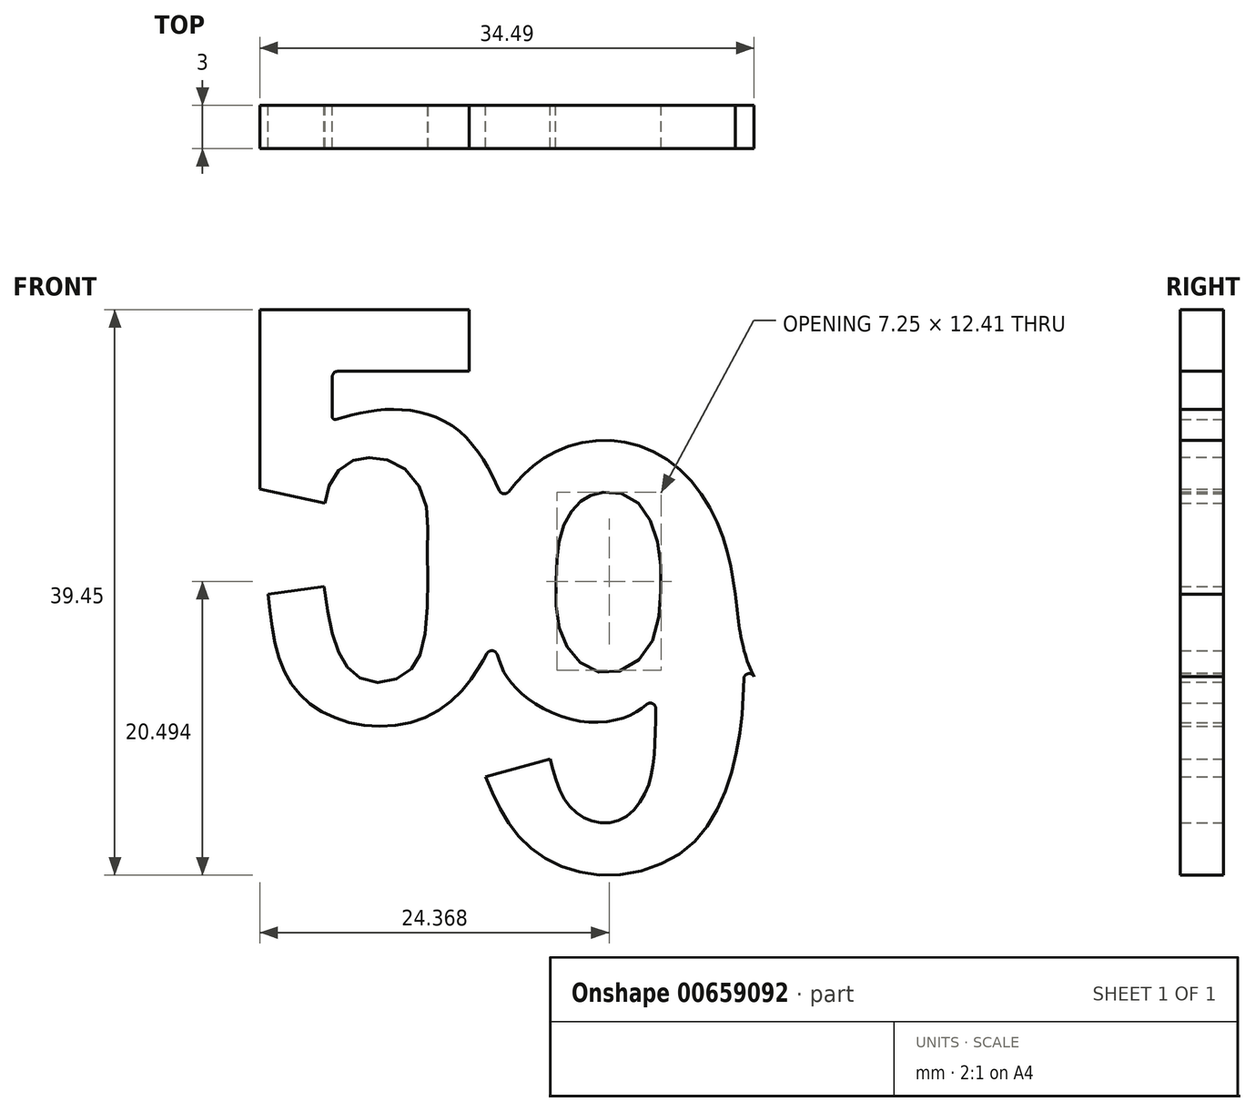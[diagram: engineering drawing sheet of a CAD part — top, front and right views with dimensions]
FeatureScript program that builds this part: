
annotation { "Feature Type Name" : "Feature", "Feature Type Description" : "" }
export const myFeature = defineFeature(function(context is Context, id is Id, definition is map)
    precondition{}
    {
        {
            var Q0;
            Q0=qCreatedBy(makeId("Front.planeOp"),FACE);
            var sketch = newSketch(context, id + "F0", { "sketchPlane" : qUnion([Q0])});
            skLineSegment(sketch, "E0", {"start": v(-24.18, 19.03) * mm, "end": v(-9.57, 19.03) * mm});
            skLineSegment(sketch, "E1", {"start": v(-24.18, 19.03) * mm, "end": v(-24.18, 6.52) * mm});
            skLineSegment(sketch, "E2", {"start": v(-24.18, 6.52) * mm, "end": v(-19.64, 5.52) * mm});
            skLineSegment(sketch, "E3", {"start": v(-9.57, 19.03) * mm, "end": v(-9.57, 14.73) * mm});
            skLineSegment(sketch, "E4", {"start": v(-9.57, 14.73) * mm, "end": v(-18.75, 14.73) * mm});
            skLineSegment(sketch, "E5", {"start": v(-19.13, 14.34) * mm, "end": v(-19.13, 11.56) * mm});
            skLineSegment(sketch, "E6", {"start": v(-19.7, -0.28) * mm, "end": v(-23.62, -0.8) * mm});
            skLineSegment(sketch, "E7", {"start": v(8.43, 19.03) * mm, "end": v(23.04, 19.03) * mm});
            skLineSegment(sketch, "E8", {"start": v(8.43, 19.03) * mm, "end": v(8.43, 6.52) * mm});
            skLineSegment(sketch, "E9", {"start": v(8.43, 6.52) * mm, "end": v(12.97, 5.52) * mm});
            skLineSegment(sketch, "E10", {"start": v(23.04, 19.03) * mm, "end": v(23.04, 14.73) * mm});
            skLineSegment(sketch, "E11", {"start": v(23.04, 14.73) * mm, "end": v(13.87, 14.73) * mm});
            skLineSegment(sketch, "E12", {"start": v(13.48, 14.34) * mm, "end": v(13.48, 11.56) * mm});
            skLineSegment(sketch, "E13", {"start": v(12.9, -0.28) * mm, "end": v(8.99, -0.8) * mm});
            skFitSpline(sketch, "E14", {"points": [v(-23.62, -0.8) * mm, v(-22.6, -5.93) * mm, v(-20.1, -8.86) * mm, v(-15.7, -10.03) * mm, v(-11.16, -8.56) * mm, v(-8.72, -5.62) * mm, v(-8.17, -4.64) * mm], "startDerivative": vector(3.05, -27.84) * mm, "endDerivative": vector(4.84, 9.1) * mm});
            skFitSpline(sketch, "E15", {"points": [v(-19.7, -0.28) * mm, v(-19.17, -3.5) * mm, v(-18.4, -5.44) * mm, v(-17.3, -6.6) * mm, v(-15.43, -6.96) * mm, v(-13.7, -6.12) * mm, v(-12.88, -4.67) * mm, v(-12.49, -0.89) * mm, v(-12.49, 3.08) * mm, v(-12.67, 5.78) * mm, v(-14.23, 8.06) * mm, v(-16.23, 8.7) * mm, v(-17.75, 8.5) * mm, v(-19.11, 7.28) * mm, v(-19.64, 5.52) * mm], "startDerivative": vector(5.37, -39.95) * mm, "endDerivative": vector(-5.42, -28.28) * mm});
            skFitSpline(sketch, "E16", {"points": [v(-19.13, 11.3) * mm, v(-16.5, 11.94) * mm, v(-13.79, 12) * mm, v(-10.94, 11.04) * mm, v(-8.67, 8.72) * mm, v(-7.35, 6.14) * mm], "startDerivative": vector(13.56, 3.87) * mm, "endDerivative": vector(5.77, -13.07) * mm});
            skFitSpline(sketch, "E17", {"points": [v(12.9, -0.28) * mm, v(13.45, -3.5) * mm, v(14.2, -5.44) * mm, v(15.31, -6.6) * mm, v(17.18, -6.96) * mm, v(18.92, -6.12) * mm, v(19.73, -4.67) * mm, v(20.13, -0.89) * mm, v(20.13, 3.08) * mm, v(19.94, 5.78) * mm, v(18.38, 8.06) * mm, v(16.39, 8.7) * mm, v(14.87, 8.5) * mm, v(13.5, 7.28) * mm, v(12.97, 5.52) * mm], "startDerivative": vector(5.37, -39.95) * mm, "endDerivative": vector(-5.42, -28.28) * mm});
            skFitSpline(sketch, "E18", {"points": [v(13.48, 11.3) * mm, v(16.1, 11.94) * mm, v(18.82, 12) * mm, v(21.67, 11.04) * mm, v(23.94, 8.72) * mm, v(25.26, 4.86) * mm, v(25.26, -0.53) * mm, v(24.45, -4.64) * mm, v(21.45, -8.56) * mm, v(16.92, -10.03) * mm, v(12.52, -8.86) * mm, v(10, -5.93) * mm, v(8.99, -0.8) * mm], "startDerivative": vector(38.15, 10.87) * mm, "endDerivative": vector(-6.34, 57.7) * mm});
            skFitSpline(sketch, "E19", {"points": [v(-6.99, 6.14) * mm, v(-5.14, 8.11) * mm, v(-2.12, 9.65) * mm, v(1.76, 9.7) * mm, v(5.68, 7.36) * mm, v(8.15, 3.12) * mm, v(8.99, -0.8) * mm], "startDerivative": vector(11.95, 14.85) * mm, "endDerivative": vector(3.37, -22.8) * mm});
            skFitSpline(sketch, "E20", {"points": [v(-7.74, -4.64) * mm, v(-7.12, -6.3) * mm, v(-5.44, -8.13) * mm, v(-1.75, -9.7) * mm, v(1.6, -9.28) * mm, v(3.17, -8.19) * mm], "startDerivative": vector(2.95, -10.23) * mm, "endDerivative": vector(7.99, 7.04) * mm});
            skFitSpline(sketch, "E21", {"points": [v(3.44, -8.19) * mm, v(3.33, -11.92) * mm, v(2.71, -14.7) * mm, v(1, -16.53) * mm, v(-1.13, -16.6) * mm, v(-2.87, -15.22) * mm, v(-3.92, -12.3) * mm], "startDerivative": vector(-0.15, -19.77) * mm, "endDerivative": vector(-4.54, 17.97) * mm});
            skLineSegment(sketch, "E22", {"start": v(-3.92, -12.3) * mm, "end": v(-8.44, -13.55) * mm});
            skFitSpline(sketch, "E23", {"points": [v(-8.44, -13.55) * mm, v(-6.76, -16.9) * mm, v(-4.1, -19.34) * mm, v(0.43, -20.41) * mm, v(5.52, -18.63) * mm, v(8.22, -14.7) * mm, v(9.4, -9.92) * mm, v(9.6, -5.93) * mm], "startDerivative": vector(11.35, -26.69) * mm, "endDerivative": vector(0.32, 28.6) * mm});
            skFitSpline(sketch, "E24", {"points": [v(-3.44, 1.62) * mm, v(-3.47, -2.1) * mm, v(-2.47, -4.9) * mm, v(0, -6.32) * mm, v(2.83, -4.74) * mm, v(3.8, -0.57) * mm, v(3.41, 3.45) * mm, v(1.7, 5.91) * mm, v(-0.47, 6.28) * mm, v(-1.4, 5.92) * mm, v(-2.26, 5.2) * mm, v(-3.07, 3.73) * mm, v(-3.44, 1.62) * mm]});
            skArc(sketch, "E25.filletArc", {"start": v(-19.13, 11.56) * mm, "mid": v(-19.05, 11.4) * mm, "end": v(-18.88, 11.37) * mm});
            skArc(sketch, "E26.filletArc", {"start": v(-7.48, 6.42) * mm, "mid": v(-7.18, 6.2) * mm, "end": v(-6.83, 6.34) * mm});
            skArc(sketch, "E27.filletArc", {"start": v(-7.62, -5.03) * mm, "mid": v(-7.95, -4.76) * mm, "end": v(-8.33, -4.96) * mm});
            skArc(sketch, "E28.filletArc", {"start": v(3.44, -8.8) * mm, "mid": v(3.22, -8.45) * mm, "end": v(2.8, -8.5) * mm});
            skArc(sketch, "E29.filletArc", {"start": v(13.48, 11.56) * mm, "mid": v(13.56, 11.4) * mm, "end": v(13.73, 11.37) * mm});
            skPoint(sketch, "E30.visualSharp", {"position": v(13.48, 14.73) * mm});
            skArc(sketch, "E30.filletArc", {"start": v(13.87, 14.73) * mm, "mid": v(13.6, 14.61) * mm, "end": v(13.48, 14.34) * mm});
            skPoint(sketch, "E31.visualSharp", {"position": v(-19.13, 14.73) * mm});
            skArc(sketch, "E31.filletArc", {"start": v(-18.75, 14.73) * mm, "mid": v(-19.02, 14.61) * mm, "end": v(-19.13, 14.34) * mm});
            skArc(sketch, "E32.filletArc", {"start": v(10.3, -6.55) * mm, "mid": v(9.88, -6.36) * mm, "end": v(9.58, -6.73) * mm});
            skSolve(sketch);
        }
        {
            var Q0;
            Q0=makeQuery(id+"F0.imprint","IMPRINT",FACE,{"disambiguationData":[TD([[makeQuery(id+"F0.imprint","IMPRINT",EDGE,{"derivedFrom":sQuery(id+"F0.wireOp",EDGE,"E0")}),-1.0]])]});
            extrude(context, id + "F1", {"entities" : qUnion([Q0]), "depth" : 3 * mm, "offsetDistance" : 25 * mm});
        }
    });
